# Revit family: KKDC_MOMO-L_P030_3000K_1010mm
name_source: partatom
category: 조명 설비
units: mm (PartAtom-declared; Revit-internal decimal feet)

## family parameters
공유 = 아니오
광원 = 예
로드될 때 보이드를 사용하여 절단 = 아니오
룸 계산 점 = 아니오
부품 유형 = 보통
원형 커넥터 치수 = 지름 사용
작업 기준면 기반 = 아니오
주석 방향 유지 = 아니오
항상 수직 = 예

## types (15) — shared parameters
Height = 31
Length = 1010  [stored 3.31365 ft]
Width = 25  [stored 0.082021 ft]
감광 램프 색상 온도 변화 = <없음>
경사도 = 90.00°
램프 = P030
렌더링 시 발산 모양 표시 = 아니오
색상 필터 = 16777215
와티지 해설 = 30W/m
직사각형 길이에서 발산 = 25  [stored 0.082021 ft]
직사각형 폭에서 발산 = 1000  [stored 3.28084 ft]
zero-valued in all types: 기본 높이

## per-type parameters (varying)
| type | 측광 웹 파일 |
| MOMO-L P030 3000K Clear + 12deg lens 1010mm | MOMO-L Clear cover P030 12deg lens.IES |
| MOMO-L P030 3000K Clear + 60deg lens 1010mm | MOMO-L Clear cover P030 60deg lens.IES |
| MOMO-L P030 3000K Clear + Spread lens 1010mm | MOMO-L Clear cover P030 Spread lens.IES |
| MOMO-L P030 3000K Clear + No lens 1010mm | MOMO-L Clear cover P030 No lens.IES |
| MOMO-L P030 3000K Clear + 25deg lens 1010mm | MOMO-L Clear cover P030 25deg lens.IES |
| MOMO-L P030 3000K Clear + Honeycomb Louvre + Spread lens 1010mm | MOMO-L Power Clear + Honeycomb Louvre P030(h-line) Spread lens.IES |
| MOMO-L P030 3000K Clear + Honeycomb Louvre + No lens 1010mm | MOMO-L Power Clear + Honeycomb Louvre P030(h-line) No lens.IES |
| MOMO-L P030 3000K Clear + Honeycomb Louvre + 60deg lens 1010mm | MOMO-L Power Clear + Honeycomb Louvre P030(h-line) 60deg lens.IES |
| MOMO-L P030 3000K Clear + Honeycomb Louvre + 12deg lens 1010mm | MOMO-L Power Clear + Honeycomb Louvre P030(h-line) 12deg lens.IES |
| MOMO-L P030 3000K Clear + Honeycomb Louvre + 25deg lens 1010mm | MOMO-L Power Clear + Honeycomb Louvre P030(h-line) Spread lens.IES |
| MOMO-L P030 3000K Clear + Micro Louvre + 12deg lens 1010mm | MOMO-L Power Clear + Micro Louvre P030(h-line) 12deg lens.IES |
| MOMO-L P030 3000K Clear + Micro Louvre + 25deg lens 1010mm | MOMO-L Power Clear + Micro Louvre P030(h-line) 25deg lens.IES |
| MOMO-L P030 3000K Clear + Micro Louvre + 60deg lens 1010mm | MOMO-L Power Clear + Micro Louvre P030(h-line) 60deg lens.IES |
| MOMO-L P030 3000K Clear + Micro Louvre + Spread lens 1010mm | MOMO-L Power Clear + Micro Louvre P030(h-line) Spread lens 510mm.IES |
| MOMO-L P030 3000K Clear + Micro Louvre + No lens 1010mm | MOMO-L Power Clear + Micro Louvre P030(h-line) No lens 510mm.IES |

note: [stored X ft] marks values corroborated as IEEE doubles in the binary element streams (Revit-internal decimal feet)
